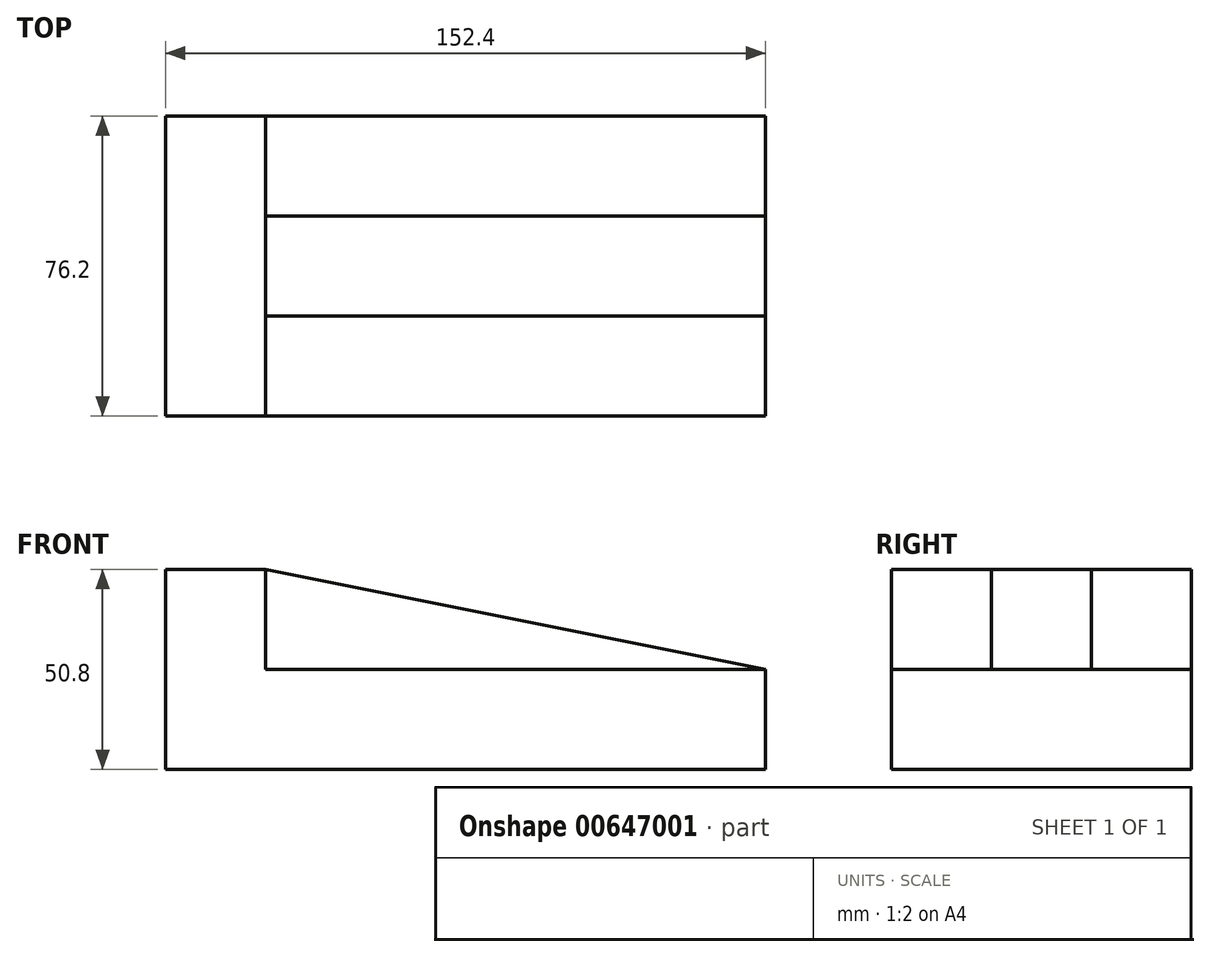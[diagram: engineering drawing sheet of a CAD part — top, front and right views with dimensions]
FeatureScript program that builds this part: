
annotation { "Feature Type Name" : "Feature", "Feature Type Description" : "" }
export const myFeature = defineFeature(function(context is Context, id is Id, definition is map)
    precondition{}
    {
        {
            var Q0;
            Q0=qCreatedBy(makeId("Front.planeOp"),FACE);
            var sketch = newSketch(context, id + "F0", { "sketchPlane" : qUnion([Q0])});
            skLineSegment(sketch, "E0", {"start": v(-60.77, 57.63) * mm, "end": v(-60.77, 6.83) * mm});
            skLineSegment(sketch, "E1", {"start": v(-60.77, 57.63) * mm, "end": v(-35.37, 57.63) * mm});
            skLineSegment(sketch, "E2", {"start": v(-35.37, 57.63) * mm, "end": v(-35.37, 32.23) * mm});
            skLineSegment(sketch, "E3", {"start": v(-35.37, 32.23) * mm, "end": v(91.63, 32.23) * mm});
            skLineSegment(sketch, "E4", {"start": v(-60.77, 6.83) * mm, "end": v(91.63, 6.83) * mm});
            skLineSegment(sketch, "E5", {"start": v(91.63, 32.23) * mm, "end": v(91.63, 6.83) * mm});
            skLineSegment(sketch, "E6", {"start": v(-35.37, 57.63) * mm, "end": v(91.63, 32.23) * mm});
            skSolve(sketch);
        }
        {
            var Q0;
            Q0=makeQuery(id+"F0.imprint","IMPRINT",FACE,{"disambiguationData":[TD([[makeQuery(id+"F0.imprint","IMPRINT",EDGE,{"derivedFrom":sQuery(id+"F0.wireOp",EDGE,"E0")}),1.0]])]});
            extrude(context, id + "F1", {"entities" : qUnion([Q0]), "oppositeDirection" : true, "depth" : 50.8 * mm, "offsetDistance" : 25.4 * mm});
        }
        {
            var Q0;
            Q0=makeQuery(id+"F0.imprint","IMPRINT",FACE,{"disambiguationData":[TD([[makeQuery(id+"F0.imprint","IMPRINT",EDGE,{"derivedFrom":sQuery(id+"F0.wireOp",EDGE,"E2")}),1.0]])]});
            extrude(context, id + "F2", {"entities" : qUnion([Q0]), "operationType" : NewBodyOperationType.ADD, "oppositeDirection" : true, "depth" : 25.4 * mm, "offsetDistance" : 25.4 * mm});
        }
        {
            var Q0;
            Q0=makeQuery(id+"F0.imprint","IMPRINT",FACE,{"disambiguationData":[TD([[makeQuery(id+"F0.imprint","IMPRINT",EDGE,{"derivedFrom":sQuery(id+"F0.wireOp",EDGE,"E0")}),1.0]])]});
            extrude(context, id + "F3", {"entities" : qUnion([Q0]), "operationType" : NewBodyOperationType.ADD, "depth" : 25.4 * mm, "offsetDistance" : 25.4 * mm});
        }
    });
